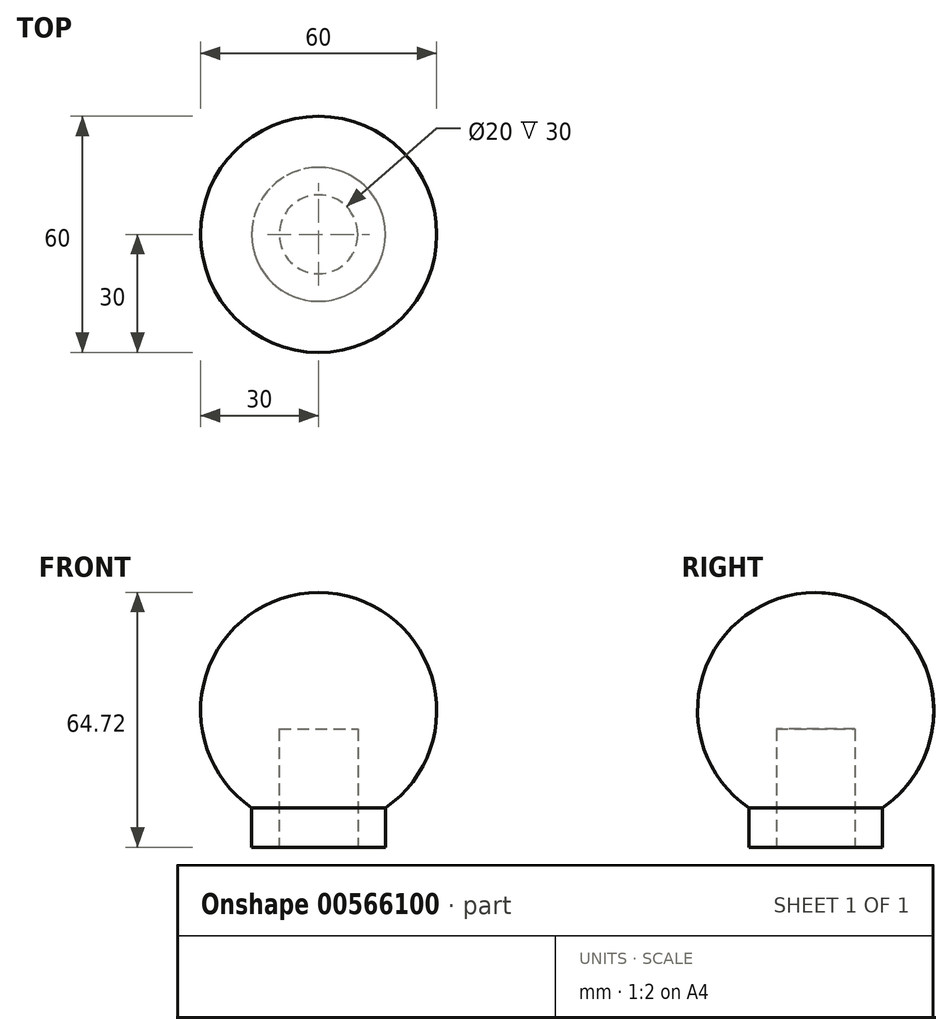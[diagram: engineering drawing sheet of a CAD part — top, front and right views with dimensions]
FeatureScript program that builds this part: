
annotation { "Feature Type Name" : "Feature", "Feature Type Description" : "" }
export const myFeature = defineFeature(function(context is Context, id is Id, definition is map)
    precondition{}
    {
        {
            var Q0;
            Q0=qCreatedBy(makeId("Right.planeOp"),FACE);
            var sketch = newSketch(context, id + "F0", { "sketchPlane" : qUnion([Q0])});
            skLineSegment(sketch, "E0", {"start": v(0, -70.05) * mm, "end": v(0, 0) * mm});
            skArc(sketch, "E1", {"start": v(17, 10) * mm, "mid": v(28.65, 43.62) * mm, "end": v(0, 64.72) * mm});
            skLineSegment(sketch, "E2", {"start": v(17, 10) * mm, "end": v(17, 0) * mm});
            skLineSegment(sketch, "E3", {"start": v(17, 0) * mm, "end": v(10, 0) * mm});
            skLineSegment(sketch, "E4", {"start": v(10, 0) * mm, "end": v(10, 30) * mm});
            skLineSegment(sketch, "E5", {"start": v(10, 30) * mm, "end": v(0, 30) * mm});
            skLineSegment(sketch, "E6", {"start": v(0, 30) * mm, "end": v(0, 64.72) * mm});
            skSolve(sketch);
        }
        {
            var Q0;
            Q0=makeQuery(id+"F0.imprint","IMPRINT",FACE,{"disambiguationData":[TD([[makeQuery(id+"F0.imprint","IMPRINT",EDGE,{"derivedFrom":sQuery(id+"F0.wireOp",EDGE,"E1")}),1.0]])]});
            var Q1;
            Q1=sQuery(id+"F0.wireOp",EDGE,"E0");
            revolve(context, id + "F1", {"entities" : qUnion([Q0]), "axis" : qUnion([Q1]), "revolveType" : RevolveType.FULL});
        }
    });
